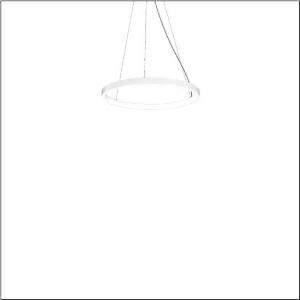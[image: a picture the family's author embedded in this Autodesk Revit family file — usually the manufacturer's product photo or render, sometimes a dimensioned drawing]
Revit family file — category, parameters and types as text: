
# Revit family: silica_21_ring-i_5pjbi1d3004a
name_source: partatom
category: Lighting Fixtures
units: mm (PartAtom-declared; Revit-internal decimal feet)

## family parameters
Cut with Voids When Loaded = No
Host = Face
Light Source = No
Part Type = Normal
Room Calculation Point = No
Round Connector Dimension = Use Diameter
Shared = No

## types (1)
- Silica 21 Ring-I (1 x LED, 3510 lm, 60 W, 4000K)
    Apparent Load = 60 VA
    CIE Flux Codes = 22 48 76 50 101
    Color Rendering = 80
    Color Temperature = 4000K
    Default Elevation = 1800 mm
    Description = Silica 21 Ring-I, suspended luminaire, of PMMA, frosted, light emission: inner ring side luminous distribution, primary light characteristic: symmetric, installation type: suspended mounting, LED, rated luminous flux: 3.510lm, luminous efficacy: 59lm/W, light colour: 840, colour temperature: 4000K, control gear: DALI 2, with terminal, 5-pole, mains connection: 230V, AC/DC, 0/50..60Hz, rated input power: 60W, housing, of extruded aluminium section, traffic white (RAL 9016), diameter: 610mm, ceiling canopy, traffic white (RAL 9016), protection rating (lamp compartment): IP40, insulation class (complete): insulation class I (protective earthing), certification: CE, impact resistance: IK02, permissible operating ambient temperature: 0..+35°C, packaging unit: 1 piece
    Height = 48 mm  [stored 0.15748 ft]
    Lamp = 1 x LED
    Lamp Light Flux = 3510 lm
    Lamp Power = 60 W
    Lamp count = 1
    Length = 610 mm
    Luminous efficacy = 59 lm/W
    Manufacturer = Siteco
    ModVariant = No
    Model = 5PJBI1D3004A
    Mounting Place = Ceiling
    Mounting Type = Pendant
    Number of Poles = 1
    OnlyDefault = Yes
    Power Factor = 1
    Product Name = Silica 21 Ring-I
    Product group = suspended luminaire
    ProductGroupID = 904
    Protection Class = Protection class I
    Protection Degree = IP 40
    RLX_Detail_Level = 1
    RLX_Emergency_Light_Flux = 0 lm
    RLX_Emergency_Type = 0
    RLX_Emergency_Type_DB = No
    RlxData = <blob elided: 10481 chars, md5=af15a782>
    Socket = socket
    Standby Power = 0 W
    System Light Flux = 3510 lm
    System Power = 60 W
    Type Comments = Product without accessories
    Type Image = l_1258363.jpg
    URL = http://relux.com
    VarID = ---
    Voltage = 0 V
    Weight = 0.00 kg
    Width = 0 mm  [stored 0 ft]

note: [stored X ft] marks values corroborated as IEEE doubles in the binary element streams (Revit-internal decimal feet)

## geometry (parser evidence)
native form markers: Sweep x14
no freeform markers — native parametric forms only
